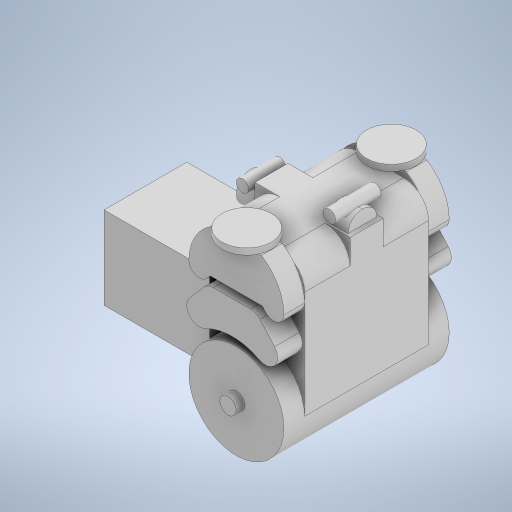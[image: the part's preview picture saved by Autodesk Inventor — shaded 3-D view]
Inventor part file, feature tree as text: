
AUTODESK INVENTOR PART (.ipt)
format: ipt  version: 2023 (Build 270158000, 158)  size: 439,808 bytes
history: native  units: in
note: dims shown in document units (in); Inventor stores cm internally (conversion verified against a paired STEP export)
features: extrude x12, sketch x11, plane x1, mirror x1
ambient origin geometry x8: Origin, YZ Plane, XZ Plane, XY Plane, X Axis, Y Axis, Z Axis, Center Point
bodies: Solid1 (feature_tree)
feature tree (25):
  extrude  "Extrusion1"  Depth=23.0in
  extrude  "Extrusion2"  Depth=32.0in
  extrude  "Extrusion4"  Depth=12.5in
  extrude  "Extrusion5"  Depth=23.0in
  extrude  "Extrusion6"  Depth=5.0in
  extrude  "Extrusion7"  Depth=3.0in
  extrude  "Extrusion8"  Depth=9.0in
  plane  "Work Plane2"
  extrude  "Extrusion9"  Depth=5.0in
  mirror  "Mirror3"
  extrude  "Extrusion10"  Depth=1.0in
  extrude  "Extrusion11"  Depth=5.0in TaperAngle=0.0deg
  extrude  "Extrusion12"  Depth=22.0in
  extrude  "Extrusion13"  Depth=6.0in TaperAngle=0.0deg
  sketch  "Sketch1"  dims[d0=23.0in d1=12.0in]
  sketch  "Sketch2"  dims[d2=12.0in d3=32.0in]
  sketch  "Sketch4"  dims[d4=15.0in d5=0.0in d6=12.5in]
  sketch  "Sketch5"  dims[d9=23.0in d10=23.0in]
  sketch  "Sketch6"  dims[d11=5.0in d12=0.0in d22=14.0in]
  sketch  "Sketch7"  dims[d23=3.0in d24=16.0in]
  sketch  "Sketch8"  dims[d25=22.0in d26=9.0in]
  sketch  "Sketch11"  dims[d27=6.0in d28=0.0in d29=5.0in]
  sketch  "Sketch12"  dims[d31=1.0in d32=1.0in]
  sketch  "Sketch13"  dims[d35=10.5in d36=5.0in d37=0.0in]
  sketch  "Sketch14"  dims[d38=4.0in d39=22.0in d41=6.0in d42=0.0in d43=12.0in d44=1.5in d45=0.0in d46=4.0in d47=2.0in d48=0.0in d50=-1.0in d51=5.0in d52=0.0in d55=11.0in d56=0.0in d57=0.0in d58=0.5in d59=3.0in d60=0.0in d61=5.0in d62=0.0in d64=0.5in d65=3.0in d66=9.0in d67=0.0in d68=6.0in d69=14.0in d70=10.0in d71=10.0in d72=42.0in d73=0.0in d74=0.5in d75=0.0344in d76=0.5in d77=0.0344in]
